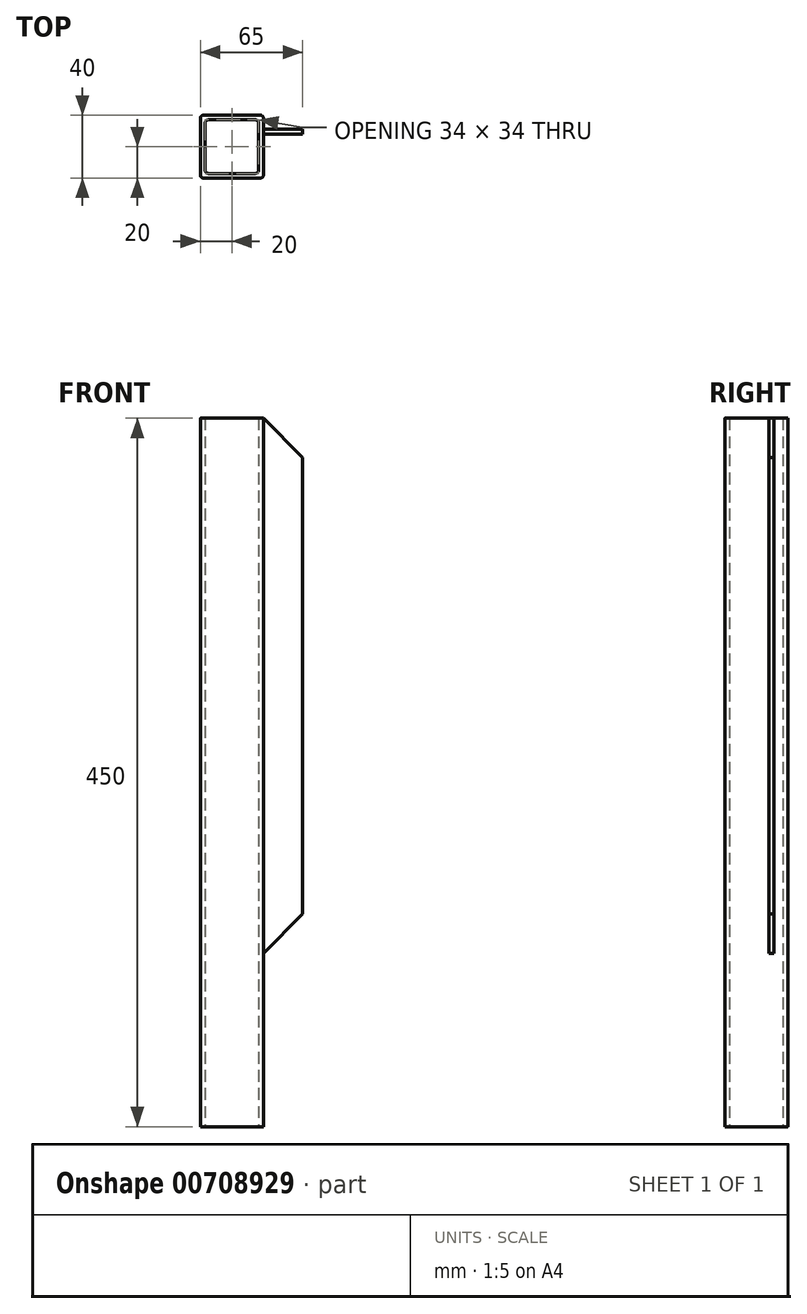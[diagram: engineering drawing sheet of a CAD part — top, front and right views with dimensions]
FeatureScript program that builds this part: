
annotation { "Feature Type Name" : "Feature", "Feature Type Description" : "" }
export const myFeature = defineFeature(function(context is Context, id is Id, definition is map)
    precondition{}
    {
        {
            var Q0;
            Q0=qCreatedBy(makeId("Top.planeOp"),FACE);
            var sketch = newSketch(context, id + "F0", { "sketchPlane" : qUnion([Q0])});
            skLineSegment(sketch, "E0.bottom", {"start": v(15, 17) * mm, "end": v(-15, 17) * mm});
            skLineSegment(sketch, "E0.top", {"start": v(15, -17) * mm, "end": v(-15, -17) * mm});
            skLineSegment(sketch, "E0.left", {"start": v(17, 15) * mm, "end": v(17, -15) * mm});
            skLineSegment(sketch, "E0.right", {"start": v(-17, 15) * mm, "end": v(-17, -15) * mm});
            skPoint(sketch, "E0.middle", {"position": v(0, 0) * mm});
            skLineSegment(sketch, "E1.0", {"start": v(18, 20) * mm, "end": v(-18, 20) * mm});
            skLineSegment(sketch, "E1.1", {"start": v(20, 18) * mm, "end": v(20, -18) * mm});
            skLineSegment(sketch, "E1.2", {"start": v(18, -20) * mm, "end": v(-18, -20) * mm});
            skLineSegment(sketch, "E1.3", {"start": v(-20, 18) * mm, "end": v(-20, -18) * mm});
            skPoint(sketch, "E2.visualSharp", {"position": v(-20, 20) * mm});
            skArc(sketch, "E2.filletArc", {"start": v(-18, 20) * mm, "mid": v(-19.41, 19.41) * mm, "end": v(-20, 18) * mm});
            skPoint(sketch, "E3.visualSharp", {"position": v(-17, 17) * mm});
            skArc(sketch, "E3.filletArc", {"start": v(-15, 17) * mm, "mid": v(-16.41, 16.41) * mm, "end": v(-17, 15) * mm});
            skPoint(sketch, "E4.visualSharp", {"position": v(17, 17) * mm});
            skArc(sketch, "E4.filletArc", {"start": v(17, 15) * mm, "mid": v(16.41, 16.41) * mm, "end": v(15, 17) * mm});
            skPoint(sketch, "E5.visualSharp", {"position": v(20, 20) * mm});
            skArc(sketch, "E5.filletArc", {"start": v(20, 18) * mm, "mid": v(19.41, 19.41) * mm, "end": v(18, 20) * mm});
            skPoint(sketch, "E6.visualSharp", {"position": v(20, -20) * mm});
            skArc(sketch, "E6.filletArc", {"start": v(18, -20) * mm, "mid": v(19.41, -19.41) * mm, "end": v(20, -18) * mm});
            skPoint(sketch, "E7.visualSharp", {"position": v(17, -17) * mm});
            skArc(sketch, "E7.filletArc", {"start": v(15, -17) * mm, "mid": v(16.41, -16.41) * mm, "end": v(17, -15) * mm});
            skPoint(sketch, "E8.visualSharp", {"position": v(-17, -17) * mm});
            skArc(sketch, "E8.filletArc", {"start": v(-17, -15) * mm, "mid": v(-16.41, -16.41) * mm, "end": v(-15, -17) * mm});
            skPoint(sketch, "E9.visualSharp", {"position": v(-20, -20) * mm});
            skArc(sketch, "E9.filletArc", {"start": v(-20, -18) * mm, "mid": v(-19.41, -19.41) * mm, "end": v(-18, -20) * mm});
            skSolve(sketch);
        }
        {
            var Q0;
            Q0=makeQuery(id+"F0.imprint","IMPRINT",FACE,{"disambiguationData":[TD([[makeQuery(id+"F0.imprint","IMPRINT",EDGE,{"derivedFrom":sQuery(id+"F0.wireOp",EDGE,"E0.bottom")}),-1.0]])]});
            var Q1;
            Q1=sQuery(id+"F0.wireOp",EDGE,"E1.0");
            extrude(context, id + "F1", {"entities" : qUnion([Q0]), "surfaceEntities" : qUnion([Q1]), "endBound" : BoundingType.SYMMETRIC, "depth" : 450 * mm, "offsetDistance" : 25 * mm});
        }
        {
            var Q0;
            Q0=makeQuery(id+"F1.opExtrude","SWEPT_FACE",FACE,{"disambiguationData":[OSD([sQuery(id+"F0.wireOp",EDGE,"E1.1")])]});
            var sketch = newSketch(context, id + "F2", { "sketchPlane" : qUnion([Q0])});
            skLineSegment(sketch, "E10.bottom", {"start": v(8, -115) * mm, "end": v(11, -115) * mm});
            skLineSegment(sketch, "E10.top", {"start": v(8, 225) * mm, "end": v(11, 225) * mm});
            skLineSegment(sketch, "E10.left", {"start": v(8, -115) * mm, "end": v(8, 225) * mm});
            skLineSegment(sketch, "E10.right", {"start": v(11, -115) * mm, "end": v(11, 225) * mm});
            skLineSegment(sketch, "E11", {"start": v(0, 225) * mm, "end": v(0, -225) * mm, "construction": true});
            skSolve(sketch);
        }
        {
            var Q0;
            Q0=makeQuery(id+"F2.imprint","IMPRINT",FACE,{"disambiguationData":[TD([[makeQuery(id+"F2.imprint","IMPRINT",EDGE,{"derivedFrom":sQuery(id+"F2.wireOp",EDGE,"E10.bottom")}),1.0]])]});
            extrude(context, id + "F3", {"entities" : qUnion([Q0]), "operationType" : NewBodyOperationType.ADD, "depth" : 25 * mm, "offsetDistance" : 25 * mm});
        }
        {
            var Q0;
            Q0=makeQuery(id+"F3.opExtrude","SWEPT_FACE",FACE,{"disambiguationData":[OSD([sQuery(id+"F2.wireOp",EDGE,"E10.left")])]});
            var sketch = newSketch(context, id + "F4", { "sketchPlane" : qUnion([Q0])});
            skLineSegment(sketch, "E12", {"start": v(20, 225) * mm, "end": v(45, 200) * mm});
            skLineSegment(sketch, "E13", {"start": v(45, 200) * mm, "end": v(20, 225) * mm});
            skLineSegment(sketch, "E14", {"start": v(45, 200) * mm, "end": v(45, 225) * mm});
            skLineSegment(sketch, "E15", {"start": v(45, 225) * mm, "end": v(20, 225) * mm});
            skLineSegment(sketch, "E16", {"start": v(45, -90) * mm, "end": v(20, -115) * mm});
            skLineSegment(sketch, "E17", {"start": v(20, -115) * mm, "end": v(45, -115) * mm});
            skLineSegment(sketch, "E18", {"start": v(45, -115) * mm, "end": v(45, -90) * mm});
            skSolve(sketch);
        }
        {
            var Q0;
            Q0=qSketchRegion(id+"F4",true);
            extrude(context, id + "F5", {"entities" : qUnion([Q0]), "operationType" : NewBodyOperationType.REMOVE, "endBound" : BoundingType.THROUGH_ALL, "oppositeDirection" : true, "depth" : 25 * mm, "offsetDistance" : 25 * mm});
        }
    });
